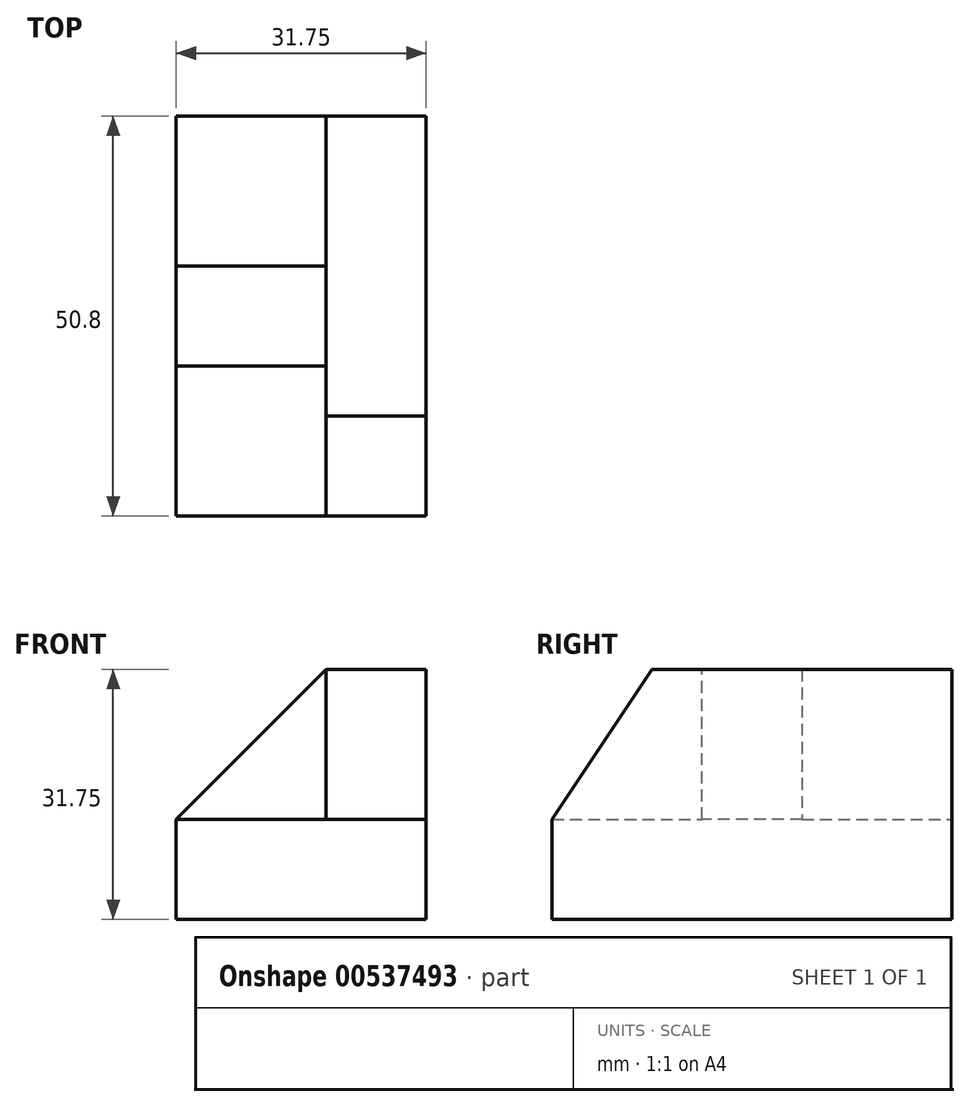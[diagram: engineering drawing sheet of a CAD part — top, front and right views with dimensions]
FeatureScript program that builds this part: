
annotation { "Feature Type Name" : "Feature", "Feature Type Description" : "" }
export const myFeature = defineFeature(function(context is Context, id is Id, definition is map)
    precondition{}
    {
        {
            var Q0;
            Q0=qCreatedBy(makeId("Right.planeOp"),FACE);
            var sketch = newSketch(context, id + "F0", { "sketchPlane" : qUnion([Q0])});
            skLineSegment(sketch, "E0", {"start": v(0, 0) * mm, "end": v(-50.8, 0) * mm});
            skLineSegment(sketch, "E1", {"start": v(-50.8, 0) * mm, "end": v(-50.8, 12.7) * mm});
            skLineSegment(sketch, "E2", {"start": v(0, 0) * mm, "end": v(0, 31.75) * mm});
            skLineSegment(sketch, "E3", {"start": v(0, 31.75) * mm, "end": v(-38.1, 31.75) * mm});
            skLineSegment(sketch, "E4", {"start": v(-38.1, 31.75) * mm, "end": v(-50.8, 12.7) * mm});
            skSolve(sketch);
        }
        {
            var Q0;
            Q0=makeQuery(id+"F0.imprint","IMPRINT",FACE,{"disambiguationData":[TD([[makeQuery(id+"F0.imprint","IMPRINT",EDGE,{"derivedFrom":sQuery(id+"F0.wireOp",EDGE,"E0")}),-1.0]])]});
            extrude(context, id + "F1", {"entities" : qUnion([Q0]), "depth" : 31.75 * mm, "offsetDistance" : 25.4 * mm});
        }
        {
            var Q0;
            Q0=makeQuery(id+"F1.opExtrude","CAP_FACE",FACE,{"disambiguationData":[OSD([sQuery(id+"F0.wireOp",EDGE,"E0"),sQuery(id+"F0.wireOp",EDGE,"E1"),sQuery(id+"F0.wireOp",EDGE,"E2"),sQuery(id+"F0.wireOp",EDGE,"E3"),sQuery(id+"F0.wireOp",EDGE,"E4")])],"isStart":true});
            var sketch = newSketch(context, id + "F2", { "sketchPlane" : qUnion([Q0])});
            skLineSegment(sketch, "E5", {"start": v(50.8, 12.7) * mm, "end": v(31.75, 12.7) * mm});
            skLineSegment(sketch, "E6", {"start": v(31.75, 12.7) * mm, "end": v(31.75, 31.75) * mm});
            skSolve(sketch);
        }
        {
            var Q0;
            Q0 = qSketchRegion(id + "F2", true);
            var Q1;
            Q1=makeQuery(id+"F2.imprint","IMPRINT",FACE,{"disambiguationData":[TD([[makeQuery(id+"F2.imprint","IMPRINT",EDGE,{"derivedFrom":sQuery(id+"F2.wireOp",EDGE,"E5")}),-1.0]])]});
            extrude(context, id + "F3", {"entities" : qUnion([Q0, Q1]), "operationType" : NewBodyOperationType.REMOVE, "oppositeDirection" : true, "depth" : 19.05 * mm, "offsetDistance" : 25.4 * mm});
        }
        {
            var Q0;
            Q0=makeQuery(id+"F3.boolean.opBoolean","COPY",FACE,{"derivedFrom":makeQuery(id+"F3.opExtrude","SWEPT_FACE",FACE,{"disambiguationData":[OSD([sQuery(id+"F2.wireOp",EDGE,"E6")])]})});
            var sketch = newSketch(context, id + "F4", { "sketchPlane" : qUnion([Q0])});
            skLineSegment(sketch, "E7", {"start": v(19.05, 31.75) * mm, "end": v(0, 12.7) * mm});
            skSolve(sketch);
        }
        {
            var Q0;
            Q0 = qSketchRegion(id + "F4", true);
            var Q1;
            Q1=makeQuery(id+"F4.imprint","IMPRINT",FACE,{"disambiguationData":[TD([[makeQuery(id+"F4.imprint","IMPRINT",EDGE,{"derivedFrom":sQuery(id+"F4.wireOp",EDGE,"E7")}),-1.0]])]});
            extrude(context, id + "F5", {"entities" : qUnion([Q0, Q1]), "operationType" : NewBodyOperationType.REMOVE, "oppositeDirection" : true, "depth" : 12.7 * mm, "offsetDistance" : 25.4 * mm});
        }
        {
            var Q0;
            Q0=makeQuery(id+"F1.opExtrude","CAP_FACE",FACE,{"disambiguationData":[OSD([sQuery(id+"F0.wireOp",EDGE,"E0"),sQuery(id+"F0.wireOp",EDGE,"E1"),sQuery(id+"F0.wireOp",EDGE,"E2"),sQuery(id+"F0.wireOp",EDGE,"E3"),sQuery(id+"F0.wireOp",EDGE,"E4")])],"isStart":true});
            var sketch = newSketch(context, id + "F6", { "sketchPlane" : qUnion([Q0])});
            skLineSegment(sketch, "E8", {"start": v(19.05, 12.7) * mm, "end": v(0, 12.7) * mm});
            skPoint(sketch, "E8.endSnap0", {"position": v(0, 15.88) * mm});
            skSolve(sketch);
        }
        {
            var Q0;
            {var subQ0=sQuery(id+"F6.wireOp",EDGE,"E8");Q0=makeQuery(id+"F6.imprint","IMPRINT",FACE,{"disambiguationData":[TD([[makeQuery(id+"F6.imprint","IMPRINT",EDGE,{"derivedFrom":subQ0}),-1.0]])]});}
            extrude(context, id + "F7", {"entities" : qUnion([Q0]), "operationType" : NewBodyOperationType.REMOVE, "oppositeDirection" : true, "depth" : 19.05 * mm, "offsetDistance" : 25.4 * mm});
        }
    });
